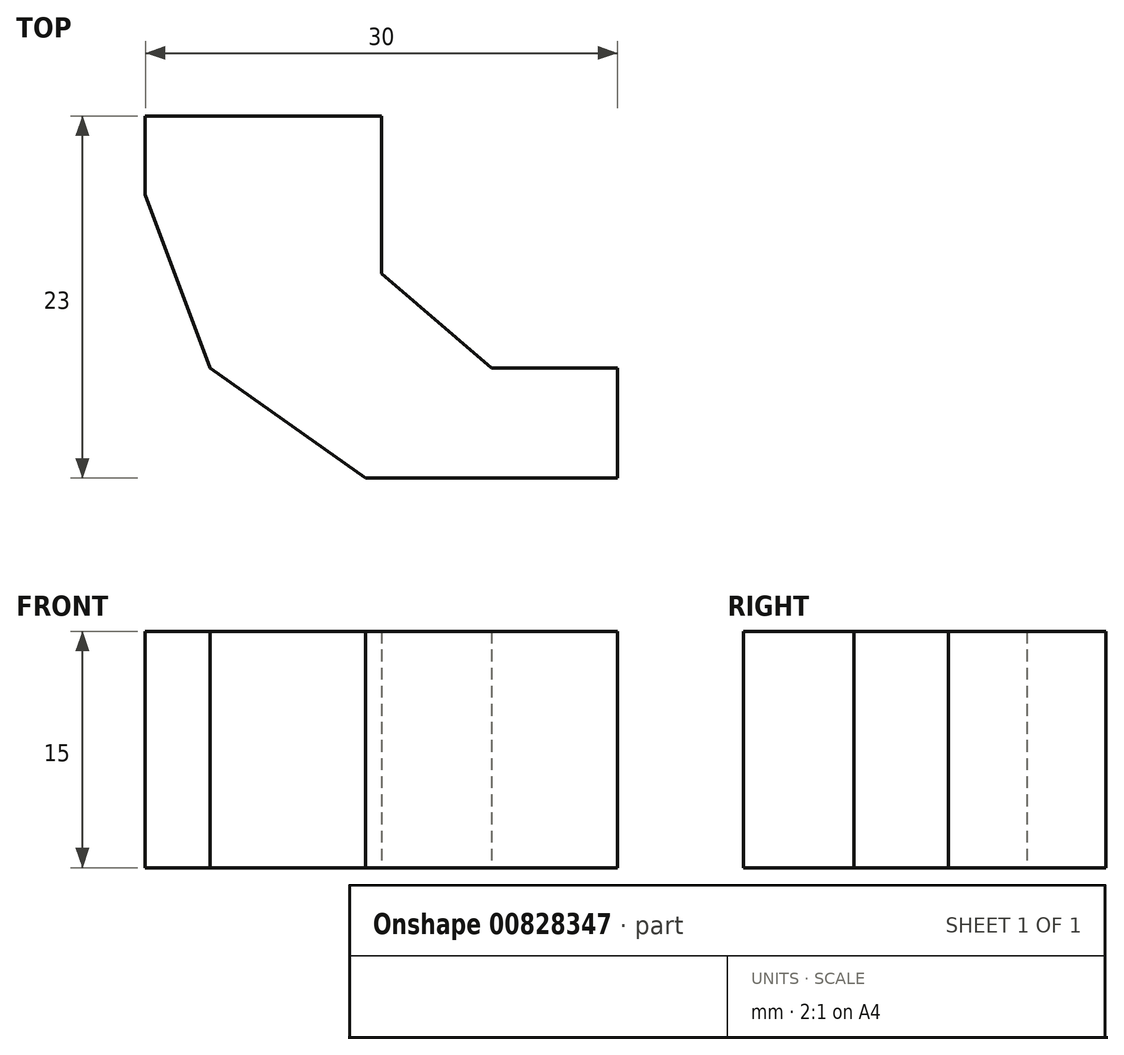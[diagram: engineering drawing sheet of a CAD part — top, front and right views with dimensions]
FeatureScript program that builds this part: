
annotation { "Feature Type Name" : "Feature", "Feature Type Description" : "" }
export const myFeature = defineFeature(function(context is Context, id is Id, definition is map)
    precondition{}
    {
        {
            var Q0;
            Q0=qCreatedBy(makeId("Top.planeOp"),FACE);
            var sketch = newSketch(context, id + "F0", { "sketchPlane" : qUnion([Q0])});
            skPoint(sketch, "E0", {"position": v(-6.11, 8.89) * mm});
            skPoint(sketch, "E1", {"position": v(-21.11, 8.89) * mm});
            skPoint(sketch, "E2", {"position": v(-21.11, 3.89) * mm});
            skPoint(sketch, "E3", {"position": v(-6.11, -1.11) * mm});
            skPoint(sketch, "E4", {"position": v(0.89, -7.11) * mm});
            skPoint(sketch, "E5", {"position": v(8.89, -7.11) * mm});
            skPoint(sketch, "E6", {"position": v(8.89, -14.11) * mm});
            skPoint(sketch, "E7", {"position": v(-7.11, -14.11) * mm});
            skPoint(sketch, "E8", {"position": v(-17.01, -7.11) * mm});
            skLineSegment(sketch, "E9", {"start": v(-21.11, 8.89) * mm, "end": v(-6.11, 8.89) * mm});
            skLineSegment(sketch, "E10", {"start": v(-6.11, -1.11) * mm, "end": v(-6.11, 8.89) * mm});
            skLineSegment(sketch, "E11", {"start": v(-6.11, -1.11) * mm, "end": v(0.89, -7.11) * mm});
            skLineSegment(sketch, "E12", {"start": v(8.89, -7.11) * mm, "end": v(0.89, -7.11) * mm});
            skLineSegment(sketch, "E13", {"start": v(8.89, -7.11) * mm, "end": v(8.89, -14.11) * mm});
            skLineSegment(sketch, "E14", {"start": v(8.89, -14.11) * mm, "end": v(-7.11, -14.11) * mm});
            skLineSegment(sketch, "E15", {"start": v(-7.11, -14.11) * mm, "end": v(-17.01, -7.11) * mm});
            skLineSegment(sketch, "E16", {"start": v(-17.01, -7.11) * mm, "end": v(-21.11, 3.89) * mm});
            skLineSegment(sketch, "E17", {"start": v(-21.11, 3.89) * mm, "end": v(-21.11, 8.89) * mm});
            skPoint(sketch, "E18", {"position": v(8.89, 8.89) * mm});
            skSolve(sketch);
        }
        {
            var Q0;
            Q0=makeQuery(id+"F0.imprint","IMPRINT",FACE,{"disambiguationData":[TD([[makeQuery(id+"F0.imprint","IMPRINT",EDGE,{"derivedFrom":sQuery(id+"F0.wireOp",EDGE,"E9")}),-1.0]])]});
            extrude(context, id + "F1", {"entities" : qUnion([Q0]), "depth" : 15 * mm, "offsetDistance" : 25 * mm});
        }
    });
